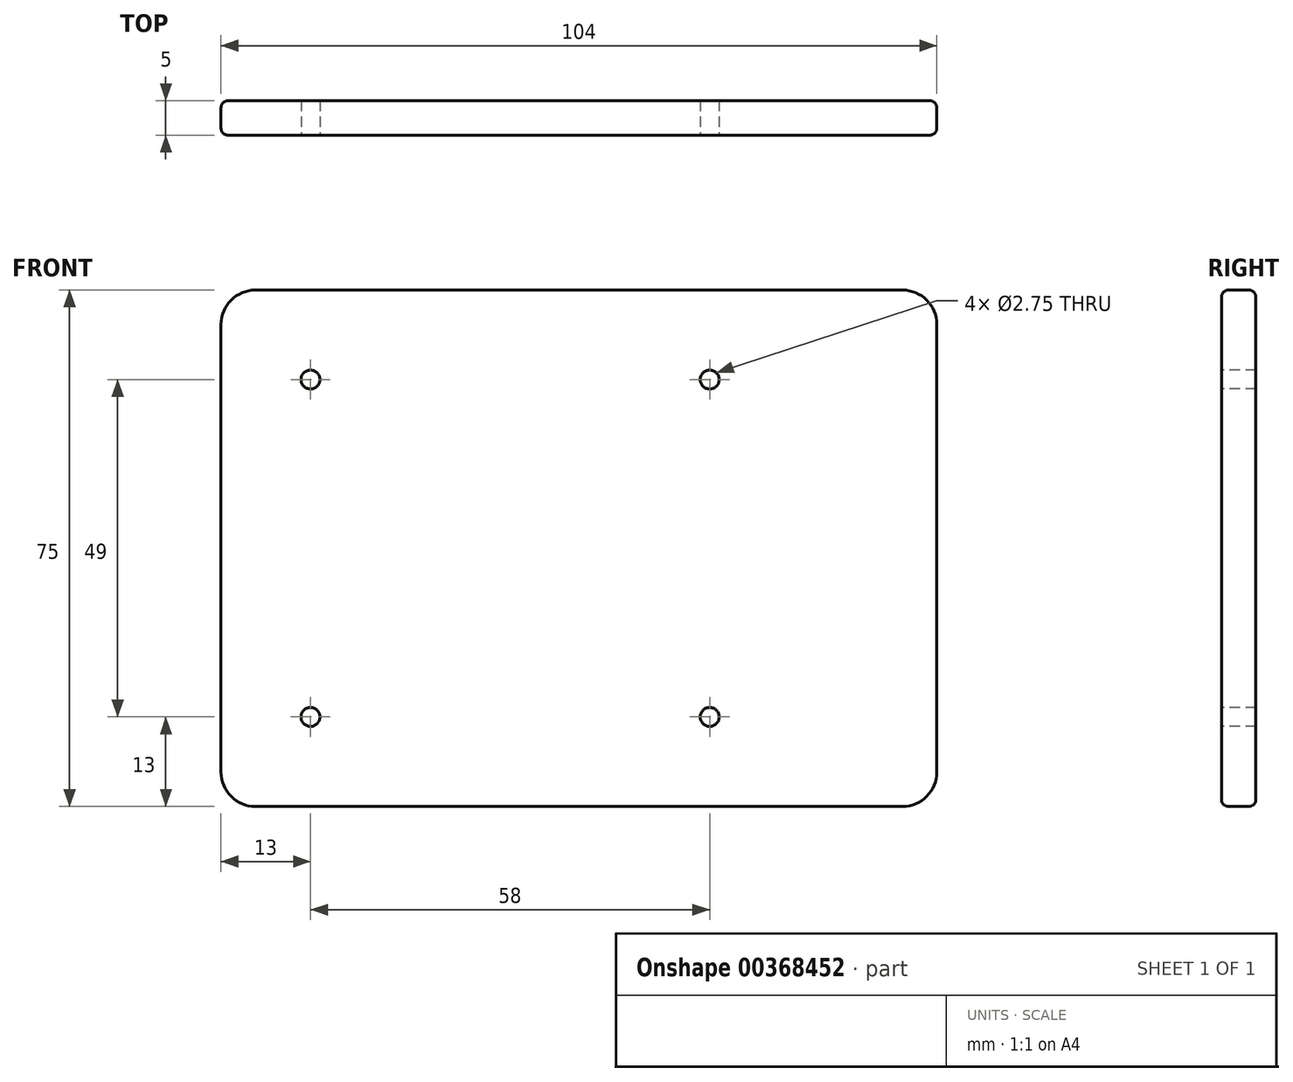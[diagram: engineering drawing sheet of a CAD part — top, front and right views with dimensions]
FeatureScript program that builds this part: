
annotation { "Feature Type Name" : "Feature", "Feature Type Description" : "" }
export const myFeature = defineFeature(function(context is Context, id is Id, definition is map)
    precondition{}
    {
        {
            var Q0;
            Q0=qCreatedBy(makeId("Front.planeOp"),FACE);
            var sketch = newSketch(context, id + "F0", { "sketchPlane" : qUnion([Q0])});
            skLineSegment(sketch, "E0.bottom", {"start": v(-52, 37.5) * mm, "end": v(52, 37.5) * mm});
            skLineSegment(sketch, "E0.top", {"start": v(-52, -37.5) * mm, "end": v(52, -37.5) * mm});
            skLineSegment(sketch, "E0.left", {"start": v(-52, 37.5) * mm, "end": v(-52, -37.5) * mm});
            skLineSegment(sketch, "E0.right", {"start": v(52, 37.5) * mm, "end": v(52, -37.5) * mm});
            skSolve(sketch);
        }
        {
            var Q0;
            Q0=makeQuery(id+"F0.imprint","IMPRINT",FACE,{"disambiguationData":[TD([[makeQuery(id+"F0.imprint","IMPRINT",EDGE,{"derivedFrom":sQuery(id+"F0.wireOp",EDGE,"E0.bottom")}),-1.0]])]});
            extrude(context, id + "F1", {"entities" : qUnion([Q0]), "oppositeDirection" : true, "depth" : 5 * mm});
        }
        {
            var Q0;
            Q0=makeQuery(id+"F1.opExtrude","SWEPT_EDGE",EDGE,{"disambiguationData":[OSD([sQuery(id+"F0.wireOp",EDGE,"E0.bottom"),sQuery(id+"F0.wireOp",EDGE,"E0.left")])]});
            var Q1;
            Q1=makeQuery(id+"F1.opExtrude","SWEPT_EDGE",EDGE,{"disambiguationData":[OSD([sQuery(id+"F0.wireOp",EDGE,"E0.bottom"),sQuery(id+"F0.wireOp",EDGE,"E0.right")])]});
            var Q2;
            Q2=makeQuery(id+"F1.opExtrude","SWEPT_EDGE",EDGE,{"disambiguationData":[OSD([sQuery(id+"F0.wireOp",EDGE,"E0.top"),sQuery(id+"F0.wireOp",EDGE,"E0.right")])]});
            var Q3;
            Q3=makeQuery(id+"F1.opExtrude","SWEPT_EDGE",EDGE,{"disambiguationData":[OSD([sQuery(id+"F0.wireOp",EDGE,"E0.top"),sQuery(id+"F0.wireOp",EDGE,"E0.left")])]});
            fillet(context, id + "F2", {"entities" : qUnion([Q0, Q1, Q2, Q3]), "radius" : 5 * mm, "tangentPropagation" : true, "allowEdgeOverflow" : false});
        }
        {
            var Q0;
            Q0=qCreatedBy(makeId("Front.planeOp"),FACE);
            var sketch = newSketch(context, id + "F3", { "sketchPlane" : qUnion([Q0])});
            skPoint(sketch, "E1", {"position": v(-39, 24.5) * mm});
            skPoint(sketch, "E2", {"position": v(19, 24.5) * mm});
            skPoint(sketch, "E3", {"position": v(-39, -24.5) * mm});
            skPoint(sketch, "E4", {"position": v(19, -24.5) * mm});
            skSolve(sketch);
        }
        {
            var Q0;
            Q0=sQuery(id+"F3.wireOp",VERTEX,"E1");
            var Q1;
            Q1=sQuery(id+"F3.wireOp",VERTEX,"E2");
            var Q2;
            Q2=sQuery(id+"F3.wireOp",VERTEX,"E4");
            var Q3;
            Q3=sQuery(id+"F3.wireOp",VERTEX,"E3");
            var Q4;
            Q4=makeQuery(id+"F1.opExtrude","SWEPT_BODY",BODY,{"disambiguationData":[OSD([sQuery(id+"F0.wireOp",EDGE,"E0.bottom"),sQuery(id+"F0.wireOp",EDGE,"E0.top"),sQuery(id+"F0.wireOp",EDGE,"E0.left"),sQuery(id+"F0.wireOp",EDGE,"E0.right")])]});
            hole(context, id + "F4", {"style" : HoleStyle.SIMPLE, "endStyle" : HoleEndStyle.THROUGH, "holeDiameter" : 2.75 * mm, "isTappedThrough" : true, "tappedDepth" : 12 * mm, "tapClearance" : 3, "locations" : qUnion([Q0, Q1, Q2, Q3]), "scope" : qUnion([Q4])});
        }
        {
            var Q0;
            Q0=makeQuery(id+"F1.opExtrude","CAP_EDGE",EDGE,{"disambiguationData":[OSD([sQuery(id+"F0.wireOp",EDGE,"E0.left")])],"isStart":false});
            fillet(context, id + "F5", {"entities" : qUnion([Q0]), "radius" : 1 * mm, "tangentPropagation" : true, "allowEdgeOverflow" : false});
        }
        {
            var Q0;
            Q0=makeQuery(id+"F1.opExtrude","CAP_EDGE",EDGE,{"disambiguationData":[OSD([sQuery(id+"F0.wireOp",EDGE,"E0.bottom")])],"isStart":true});
            fillet(context, id + "F6", {"entities" : qUnion([Q0]), "radius" : 1 * mm, "tangentPropagation" : true, "allowEdgeOverflow" : false});
        }
    });
